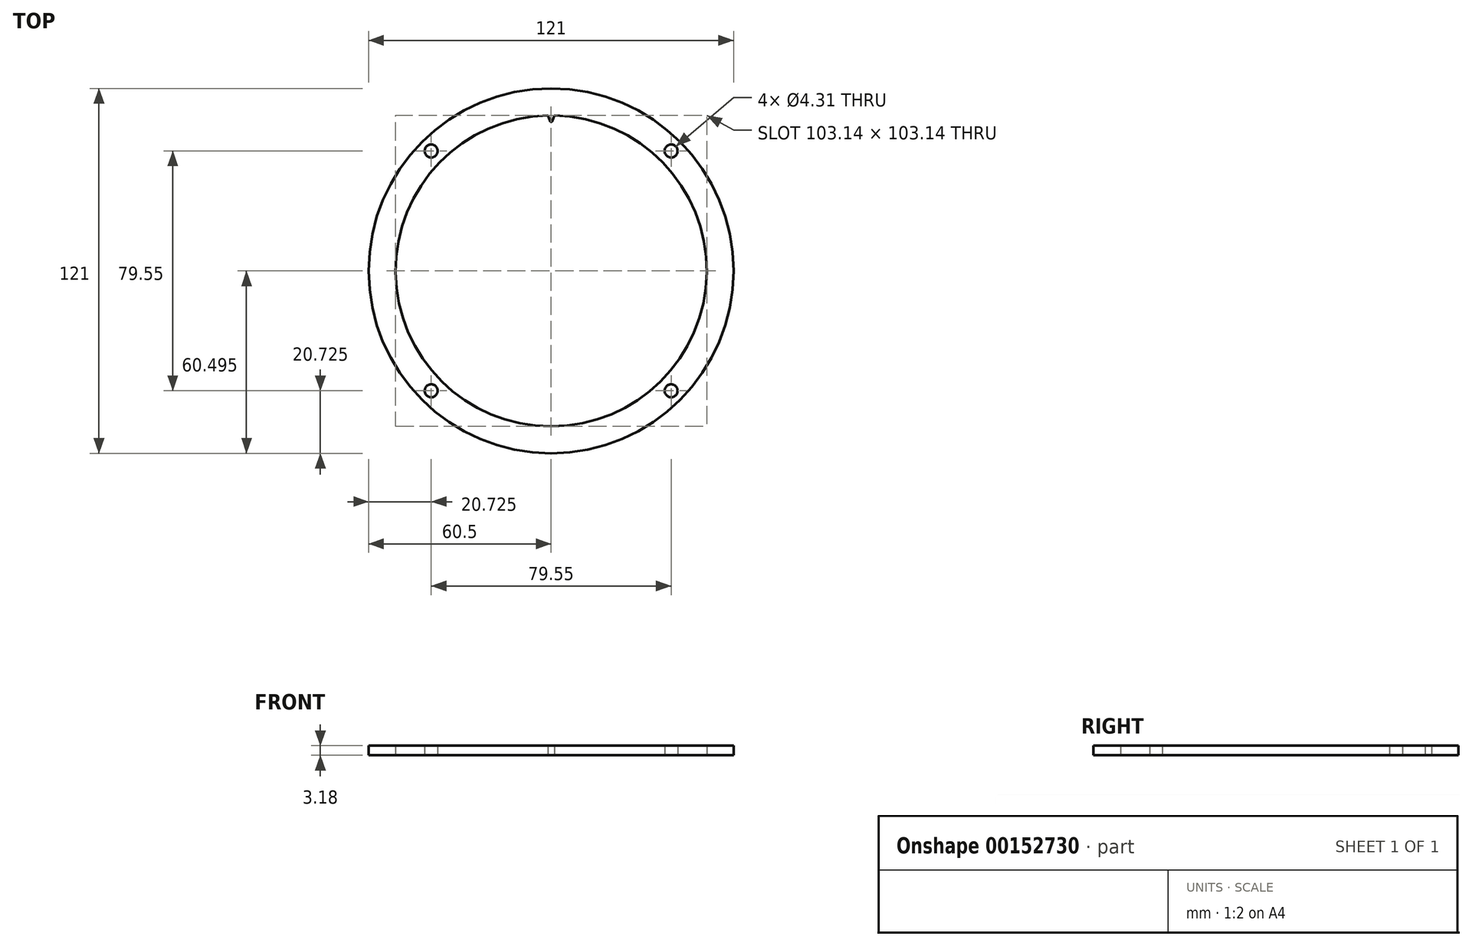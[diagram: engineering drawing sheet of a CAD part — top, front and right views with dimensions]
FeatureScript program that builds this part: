
annotation { "Feature Type Name" : "Feature", "Feature Type Description" : "" }
export const myFeature = defineFeature(function(context is Context, id is Id, definition is map)
    precondition{}
    {
        {
            var Q0;
            Q0=qCreatedBy(makeId("Top.planeOp"),FACE);
            var sketch = newSketch(context, id + "F0", { "sketchPlane" : qUnion([Q0])});
            skCircle(sketch, "E0", {"center": v(0, 0) * mm, "radius": 51.57 * mm});
            skSolve(sketch);
        }
        {
            var Q0;
            Q0 = qSketchRegion(id + "F0", true);
            extrude(context, id + "F1", {"entities" : qUnion([Q0]), "depth" : 3.17 * mm});
        }
        {
            var Q0;
            Q0=makeQuery(id+"F1.opExtrude","CAP_FACE",FACE,{"disambiguationData":[OSD([sQuery(id+"F0.wireOp",EDGE,"E0")])],"isStart":false});
            var sketch = newSketch(context, id + "F2", { "sketchPlane" : qUnion([Q0])});
            skLineSegment(sketch, "E1", {"start": v(0, 0) * mm, "end": v(0, 51.57) * mm, "construction": true});
            skLineSegment(sketch, "E2", {"start": v(0, 0) * mm, "end": v(0.66, 51.57) * mm, "construction": true});
            skArc(sketch, "E3", {"start": v(1.02, 51.56) * mm, "mid": v(0, 51.57) * mm, "end": v(-1.02, 51.56) * mm});
            skLineSegment(sketch, "E4", {"start": v(-1.02, 51.56) * mm, "end": v(-0.28, 49.6) * mm});
            skLineSegment(sketch, "E5", {"start": v(1.02, 51.56) * mm, "end": v(0.28, 49.6) * mm});
            skArc(sketch, "E6", {"start": v(-0.28, 49.6) * mm, "mid": v(0, 49.4) * mm, "end": v(0.28, 49.6) * mm});
            skPoint(sketch, "E7", {"position": v(0.65, 50.58) * mm});
            skSolve(sketch);
        }
        {
            var Q0;
            Q0 = qSketchRegion(id + "F2", true);
            var Q1;
            Q1=makeQuery(id+"F1.opExtrude","CAP_FACE",FACE,{"disambiguationData":[OSD([sQuery(id+"F0.wireOp",EDGE,"E0")])],"isStart":true});
            extrude(context, id + "F3", {"entities" : qUnion([Q0]), "operationType" : NewBodyOperationType.REMOVE, "endBound" : BoundingType.UP_TO_SURFACE, "oppositeDirection" : true, "endBoundEntityFace" : qUnion([Q1]), "depth" : 25.4 * mm});
        }
        {
            var Q0;
            Q0=makeQuery(id+"F1.opExtrude","CAP_FACE",FACE,{"disambiguationData":[OSD([sQuery(id+"F0.wireOp",EDGE,"E0")])],"isStart":false});
            var sketch = newSketch(context, id + "F4", { "sketchPlane" : qUnion([Q0])});
            skCircle(sketch, "E8", {"center": v(0, 0) * mm, "radius": 60.5 * mm});
            skLineSegment(sketch, "E9.bottom", {"start": v(39.77, 39.77) * mm, "end": v(-39.77, 39.77) * mm, "construction": true});
            skLineSegment(sketch, "E9.top", {"start": v(39.77, -39.77) * mm, "end": v(-39.77, -39.77) * mm, "construction": true});
            skLineSegment(sketch, "E9.left", {"start": v(39.77, 39.77) * mm, "end": v(39.77, -39.77) * mm, "construction": true});
            skLineSegment(sketch, "E9.right", {"start": v(-39.77, 39.77) * mm, "end": v(-39.77, -39.77) * mm, "construction": true});
            skCircle(sketch, "E10", {"center": v(39.77, 39.77) * mm, "radius": 4.25 * mm, "construction": true});
            skCircle(sketch, "E11", {"center": v(-39.77, 39.77) * mm, "radius": 2.15 * mm});
            skCircle(sketch, "E12", {"center": v(39.77, 39.77) * mm, "radius": 2.15 * mm});
            skCircle(sketch, "E13", {"center": v(39.77, -39.77) * mm, "radius": 2.15 * mm});
            skCircle(sketch, "E14", {"center": v(-39.77, -39.77) * mm, "radius": 2.15 * mm});
            skSolve(sketch);
        }
        {
            var Q0;
            Q0=makeQuery(id+"F4.imprint","IMPRINT",FACE,{"disambiguationData":[TD([[makeQuery(id+"F4.imprint","IMPRINT",EDGE,{"derivedFrom":sQuery(id+"F4.wireOp",EDGE,"E8")}),1.0]])]});
            extrude(context, id + "F5", {"entities" : qUnion([Q0]), "depth" : 3.17 * mm});
        }
        {
            var Q0;
            Q0=makeQuery(id+"F1.opExtrude","CAP_FACE",FACE,{"disambiguationData":[OSD([sQuery(id+"F0.wireOp",EDGE,"E0")])],"isStart":true});
            var Q1;
            Q1=makeQuery(id+"F5.opExtrude","CAP_FACE",FACE,{"disambiguationData":[OSD([sQuery(id+"F0.wireOp",EDGE,"E0"),sQuery(id+"F2.wireOp",EDGE,"E4"),sQuery(id+"F2.wireOp",EDGE,"E5"),sQuery(id+"F2.wireOp",EDGE,"E6"),sQuery(id+"F4.wireOp",EDGE,"E8"),sQuery(id+"F4.wireOp",EDGE,"E11"),sQuery(id+"F4.wireOp",EDGE,"E12"),sQuery(id+"F4.wireOp",EDGE,"E13"),sQuery(id+"F4.wireOp",EDGE,"E14")])],"isStart":true});
            extrude(context, id + "F6", {"entities" : qUnion([Q0]), "operationType" : NewBodyOperationType.REMOVE, "endBound" : BoundingType.UP_TO_SURFACE, "oppositeDirection" : true, "endBoundEntityFace" : qUnion([Q1]), "depth" : 25.4 * mm});
        }
    });
